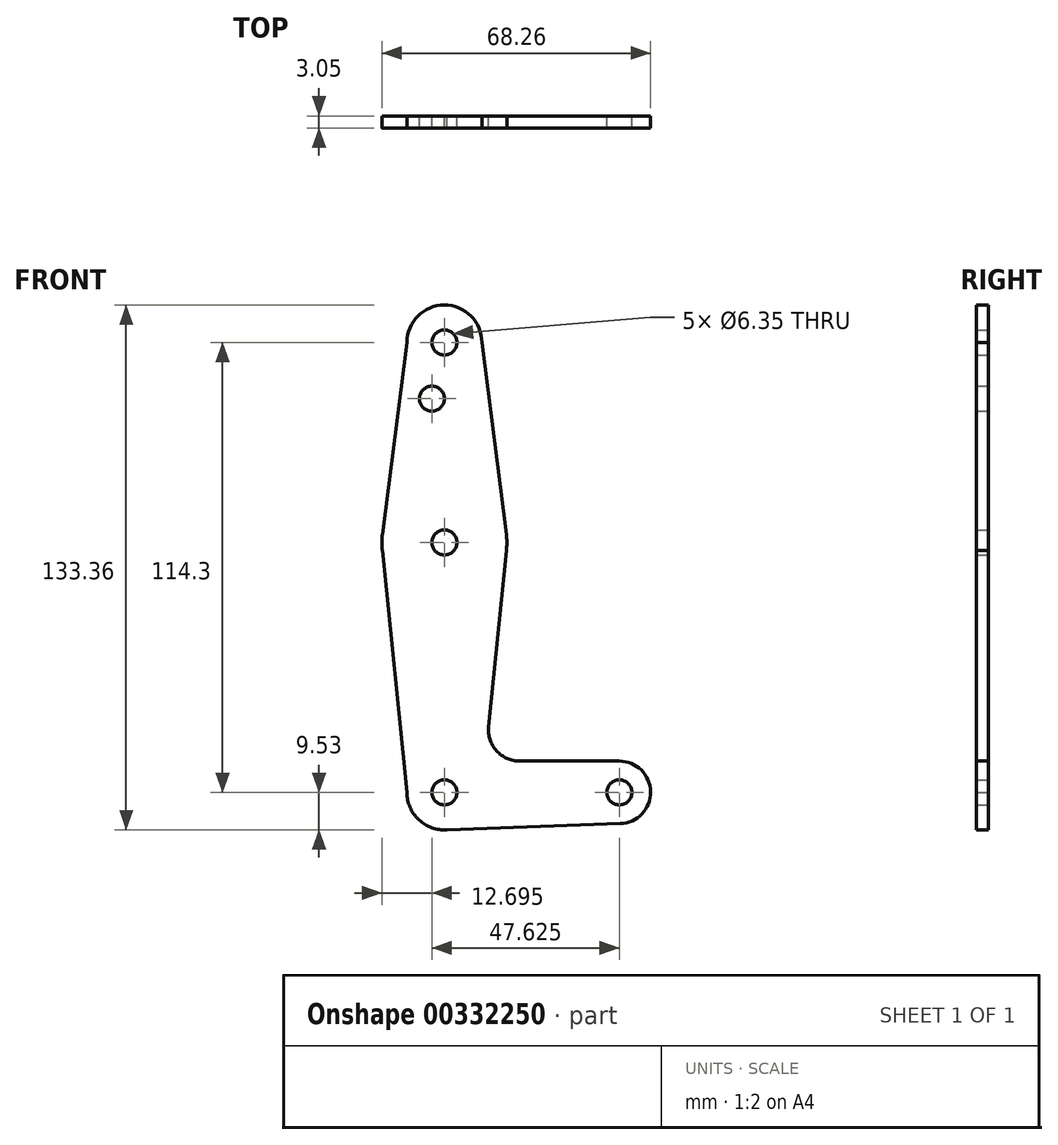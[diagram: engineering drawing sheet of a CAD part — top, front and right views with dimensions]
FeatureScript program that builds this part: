
annotation { "Feature Type Name" : "Feature", "Feature Type Description" : "" }
export const myFeature = defineFeature(function(context is Context, id is Id, definition is map)
    precondition{}
    {
        {
            var Q0;
            Q0=qCreatedBy(makeId("Front.planeOp"),FACE);
            var sketch = newSketch(context, id + "F0", { "sketchPlane" : qUnion([Q0])});
            skLineSegment(sketch, "E0", {"start": v(0, 114.3) * mm, "end": v(0, 0) * mm, "construction": true});
            skLineSegment(sketch, "E1", {"start": v(0, 0) * mm, "end": v(44.45, 0) * mm, "construction": true});
            skCircle(sketch, "E2", {"center": v(0, 114.3) * mm, "radius": 9.53 * mm});
            skCircle(sketch, "E3", {"center": v(0, 63.5) * mm, "radius": 15.88 * mm});
            skCircle(sketch, "E4", {"center": v(0, 0) * mm, "radius": 9.53 * mm});
            skCircle(sketch, "E5", {"center": v(44.45, 0) * mm, "radius": 7.94 * mm});
            skLineSegment(sketch, "E6", {"start": v(19.16, 7.94) * mm, "end": v(44.45, 7.94) * mm});
            skLineSegment(sketch, "E7", {"start": v(-9.53, 114.3) * mm, "end": v(-15.75, 65.5) * mm});
            skLineSegment(sketch, "E8", {"start": v(9.52, 114.3) * mm, "end": v(15.75, 65.5) * mm});
            skLineSegment(sketch, "E9", {"start": v(-15.75, 61.5) * mm, "end": v(-9.53, 0) * mm});
            skLineSegment(sketch, "E10", {"start": v(15.75, 61.5) * mm, "end": v(11.25, 16.68) * mm});
            skLineSegment(sketch, "E11", {"start": v(0, -9.53) * mm, "end": v(44.73, -7.93) * mm});
            skCircle(sketch, "E12", {"center": v(0, 114.3) * mm, "radius": 3.18 * mm});
            skCircle(sketch, "E13", {"center": v(-3.17, 100.03) * mm, "radius": 3.18 * mm});
            skCircle(sketch, "E14", {"center": v(0, 63.5) * mm, "radius": 3.18 * mm});
            skCircle(sketch, "E15", {"center": v(0, 0) * mm, "radius": 3.18 * mm});
            skCircle(sketch, "E16", {"center": v(44.45, 0) * mm, "radius": 3.18 * mm});
            skArc(sketch, "E17.filletArc", {"start": v(11.25, 16.68) * mm, "mid": v(13.26, 10.55) * mm, "end": v(19.16, 7.94) * mm});
            skSolve(sketch);
        }
        {
            var Q0;
            Q0 = qSketchRegion(id + "F0", true);
            extrude(context, id + "F1", {"entities" : qUnion([Q0]), "depth" : 3.05 * mm});
        }
    });
